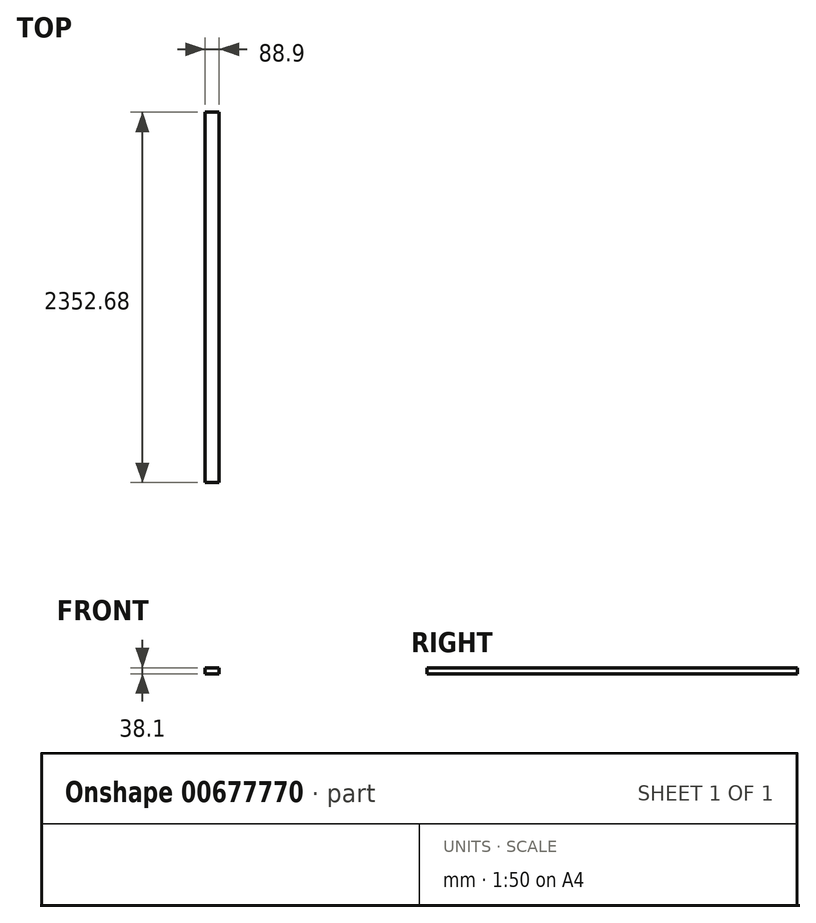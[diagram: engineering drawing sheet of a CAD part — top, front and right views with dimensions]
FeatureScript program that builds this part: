
annotation { "Feature Type Name" : "Feature", "Feature Type Description" : "" }
export const myFeature = defineFeature(function(context is Context, id is Id, definition is map)
    precondition{}
    {
        {
            var Q0;
            Q0=qCreatedBy(makeId("Front.planeOp"),FACE);
            var sketch = newSketch(context, id + "F0", { "sketchPlane" : qUnion([Q0])});
            skLineSegment(sketch, "E0.bottom", {"start": v(16, -127.8) * mm, "end": v(-72.9, -127.8) * mm});
            skLineSegment(sketch, "E0.top", {"start": v(16, -89.7) * mm, "end": v(-72.9, -89.7) * mm});
            skLineSegment(sketch, "E0.left", {"start": v(16, -127.8) * mm, "end": v(16, -89.7) * mm});
            skLineSegment(sketch, "E0.right", {"start": v(-72.9, -127.8) * mm, "end": v(-72.9, -89.7) * mm});
            skPoint(sketch, "E0.middle", {"position": v(-28.46, -108.76) * mm});
            skSolve(sketch);
        }
        {
            var Q0;
            Q0 = qSketchRegion(id + "F0", true);
            extrude(context, id + "F1", {"entities" : qUnion([Q0]), "depth" : 2352.67 * mm, "offsetDistance" : 25.4 * mm});
        }
    });
